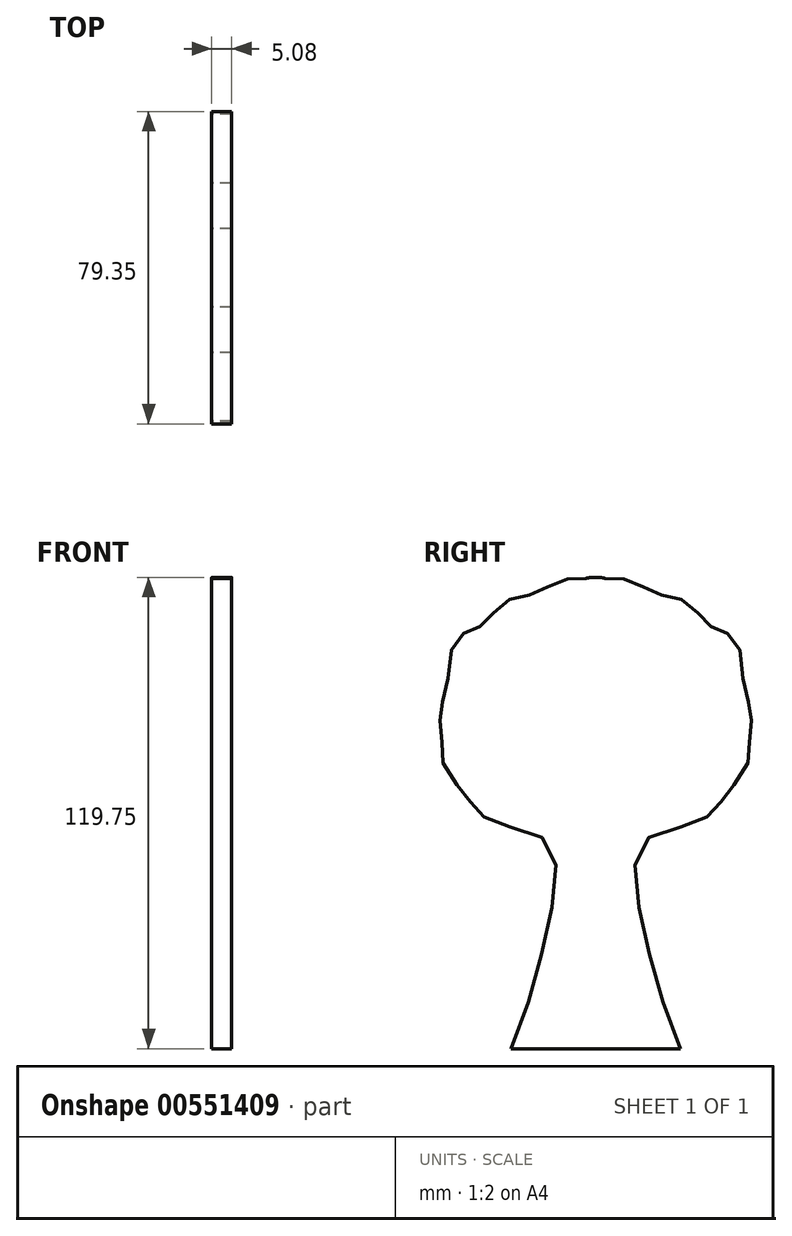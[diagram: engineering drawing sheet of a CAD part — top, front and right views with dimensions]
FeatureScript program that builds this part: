
annotation { "Feature Type Name" : "Feature", "Feature Type Description" : "" }
export const myFeature = defineFeature(function(context is Context, id is Id, definition is map)
    precondition{}
    {
        {
            var Q0;
            Q0=qCreatedBy(makeId("Right.planeOp"),FACE);
            var sketch = newSketch(context, id + "F0", { "sketchPlane" : qUnion([Q0])});
            skLineSegment(sketch, "E0", {"start": v(-56.39, 209.18) * mm, "end": v(-45.64, 209.18) * mm});
            skPoint(sketch, "E1", {"position": v(-45.64, 209.18) * mm});
            skPoint(sketch, "E2", {"position": v(-24.13, 209.18) * mm});
            skLineSegment(sketch, "E3", {"start": v(-24.13, 209.18) * mm, "end": v(-13.38, 209.18) * mm});
            skPoint(sketch, "E4.start.orphan", {"position": v(-34.89, 209.18) * mm});
            skFitSpline(sketch, "E5.MirrorCS", {"points": [v(-13.38, 209.18) * mm, v(-22.96, 241.07) * mm, v(-22.78, 261.64) * mm, v(-9.28, 266.64) * mm, v(-4.01, 270.67) * mm, v(-0.45, 275.26) * mm, v(4.11, 282.67) * mm, v(4.11, 288.39) * mm, v(4.75, 294.86) * mm, v(3.05, 299.78) * mm, v(1.7, 310.64) * mm, v(-1.87, 314.97) * mm, v(-5.87, 316.68) * mm, v(-9.35, 320.4) * mm, v(-14.34, 323.87) * mm, v(-19.82, 324.8) * mm, v(-24.77, 327.7) * mm, v(-30.71, 328.69) * mm, v(-34.89, 330.75) * mm], "startDerivative": vector(-121.18, 275.73) * mm, "endDerivative": vector(-114.53, 172.82) * mm});
            skLineSegment(sketch, "E6", {"start": v(-34.89, 196.48) * mm, "end": v(-34.89, 322) * mm, "construction": true});
            skFitSpline(sketch, "E7.MirrorCS", {"points": [v(-56.39, 209.18) * mm, v(-46.81, 241.07) * mm, v(-47, 261.64) * mm, v(-60.5, 266.64) * mm, v(-65.76, 270.67) * mm, v(-69.32, 275.26) * mm, v(-73.88, 282.67) * mm, v(-73.88, 288.39) * mm, v(-74.52, 294.86) * mm, v(-72.82, 299.78) * mm, v(-71.47, 310.64) * mm, v(-67.9, 314.97) * mm, v(-63.9, 316.68) * mm, v(-60.42, 320.4) * mm, v(-55.43, 323.87) * mm, v(-49.95, 324.8) * mm, v(-45, 327.7) * mm, v(-39.06, 328.69) * mm, v(-34.89, 330.75) * mm], "startDerivative": vector(121.18, 275.73) * mm, "endDerivative": vector(114.53, 172.82) * mm});
            skLineSegment(sketch, "E8", {"start": v(-24.13, 209.18) * mm, "end": v(-45.64, 209.18) * mm});
            skSolve(sketch);
        }
        {
            var Q0;
            Q0=makeQuery(id+"F0.imprint","IMPRINT",FACE,{"disambiguationData":[TD([[makeQuery(id+"F0.imprint","IMPRINT",EDGE,{"derivedFrom":sQuery(id+"F0.wireOp",EDGE,"E0")}),1.0]])]});
            extrude(context, id + "F1", {"entities" : qUnion([Q0]), "depth" : 5.08 * mm, "offsetDistance" : 25.4 * mm});
        }
        {
            var Q0;
            Q0=makeQuery(id+"F1.opExtrude","SWEPT_EDGE",EDGE,{"disambiguationData":[OSD([sQuery(id+"F0.wireOp",EDGE,"E5.MirrorCS"),sQuery(id+"F0.wireOp",EDGE,"E7.MirrorCS")])]});
            fillet(context, id + "F2", {"entities" : qUnion([Q0]), "radius" : 12.85 * mm, "tangentPropagation" : true, "allowEdgeOverflow" : false});
        }
    });
